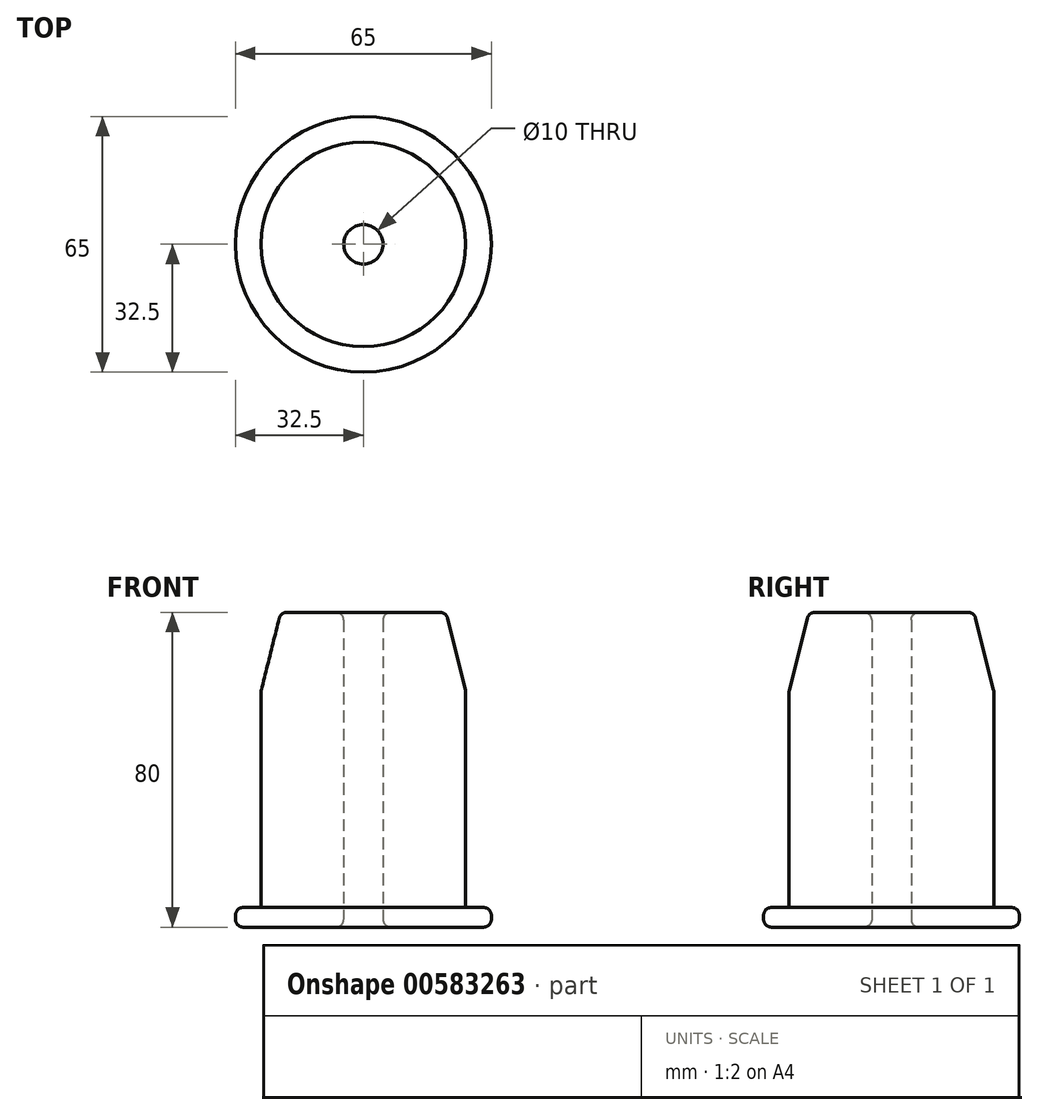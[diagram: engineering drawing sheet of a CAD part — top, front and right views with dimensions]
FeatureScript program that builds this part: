
annotation { "Feature Type Name" : "Feature", "Feature Type Description" : "" }
export const myFeature = defineFeature(function(context is Context, id is Id, definition is map)
    precondition{}
    {
        {
            var Q0;
            Q0=qCreatedBy(makeId("Right.planeOp"),FACE);
            var sketch = newSketch(context, id + "F0", { "sketchPlane" : qUnion([Q0])});
            skCircle(sketch, "E0", {"center": v(0, 0) * mm, "radius": 26 * mm});
            skCircle(sketch, "E1", {"center": v(0, 0) * mm, "radius": 5 * mm});
            skLineSegment(sketch, "E2", {"start": v(0, 0) * mm, "end": v(48.45, 0) * mm});
            skSolve(sketch);
        }
        {
            var Q0;
            Q0=makeQuery(id+"F0.imprint","IMPRINT",FACE,{"disambiguationData":[TD([[makeQuery(id+"F0.imprint","IMPRINT",EDGE,{"derivedFrom":sQuery(id+"F0.wireOp",EDGE,"E0")}),1.0]])]});
            extrude(context, id + "F1", {"entities" : qUnion([Q0]), "endBound" : BoundingType.SYMMETRIC, "depth" : 75 * mm, "offsetDistance" : 25 * mm});
        }
        {
            var Q0;
            Q0=makeQuery(id+"F1.opExtrude","CAP_FACE",FACE,{"disambiguationData":[OSD([sQuery(id+"F0.wireOp",EDGE,"E0"),sQuery(id+"F0.wireOp",EDGE,"E1")])],"isStart":true});
            var sketch = newSketch(context, id + "F2", { "sketchPlane" : qUnion([Q0])});
            skCircle(sketch, "E3", {"center": v(0, 0) * mm, "radius": 32.5 * mm});
            skSolve(sketch);
        }
        {
            var Q0;
            Q0=makeQuery(id+"F2.imprint","IMPRINT",FACE,{"disambiguationData":[TD([[makeQuery(id+"F2.imprint","IMPRINT",EDGE,{"derivedFrom":sQuery(id+"F2.wireOp",EDGE,"E3")}),1.0]])]});
            var Q1;
            Q1=makeQuery(id+"F2.imprint","IMPRINT",FACE,{"disambiguationData":[TD([[makeQuery(id+"F2.imprint","IMPRINT",EDGE,{"derivedFrom":makeQuery(id+"F1.opExtrude","CAP_EDGE",EDGE,{"disambiguationData":[OSD([sQuery(id+"F0.wireOp",EDGE,"E0")])],"isStart":true})}),-1.0]])]});
            extrude(context, id + "F3", {"entities" : qUnion([Q0, Q1]), "operationType" : NewBodyOperationType.ADD, "depth" : 5 * mm, "offsetDistance" : 25 * mm});
        }
        {
            var Q0;
            Q0=makeQuery(id+"F1.opExtrude","CAP_EDGE",EDGE,{"disambiguationData":[OSD([sQuery(id+"F0.wireOp",EDGE,"E0")])],"isStart":false});
            chamfer(context, id + "F4", {"entities" : qUnion([Q0]), "chamferType" : ChamferType.TWO_OFFSETS, "width1" : 5 * mm, "oppositeDirection" : false, "width2" : 20 * mm, "tangentPropagation" : true});
        }
        {
            var Q0;
            Q0=makeQuery(id+"F3.opExtrude","CAP_FACE",FACE,{"disambiguationData":[OSD([sQuery(id+"F0.wireOp",EDGE,"E1"),sQuery(id+"F2.wireOp",EDGE,"E3")])],"isStart":false});
            var Q1;
            Q1=makeQuery(id+"F3.opExtrude","CAP_EDGE",EDGE,{"disambiguationData":[OSD([sQuery(id+"F2.wireOp",EDGE,"E3")])],"isStart":true});
            var Q2;
            Q2=makeQuery(id+"F1.opExtrude","CAP_FACE",FACE,{"disambiguationData":[OSD([sQuery(id+"F0.wireOp",EDGE,"E0"),sQuery(id+"F0.wireOp",EDGE,"E1")])],"isStart":false});
            var Q3;
            {var subQ0=sQuery(id+"F0.wireOp",EDGE,"E0");Q3=makeQuery(id+"F4.opChamfer","BLEND_EDGE",EDGE,{"blendedFrom":[makeQuery(id+"F1.opExtrude","CAP_EDGE",EDGE,{"disambiguationData":[OSD([subQ0])],"isStart":false}),makeQuery(id+"F1.opExtrude","SWEPT_FACE",FACE,{"disambiguationData":[OSD([subQ0])]})],"blendedInto":[makeQuery(id+"F1.opExtrude","SWEPT_FACE",FACE,{"disambiguationData":[OSD([subQ0])]})]});}
            fillet(context, id + "F5", {"entities" : qUnion([Q0, Q1, Q2, Q3]), "radius" : 2 * mm, "tangentPropagation" : true, "allowEdgeOverflow" : false});
        }
        {
            var Q0;
            Q0=makeQuery(id+"F1.opExtrude","SWEPT_BODY",BODY,{"disambiguationData":[OSD([sQuery(id+"F0.wireOp",EDGE,"E0"),sQuery(id+"F0.wireOp",EDGE,"E1")])]});
            var Q1;
            Q1=sQuery(id+"F0.wireOp",EDGE,"E2");
            transform(context, id + "F6", {"entities" : qUnion([Q0]), "transformType" : TransformType.ROTATION, "transformAxis" : qUnion([Q1]), "angle" : 90 * degree, "oppositeDirection" : true, "makeCopy" : false});
        }
    });
